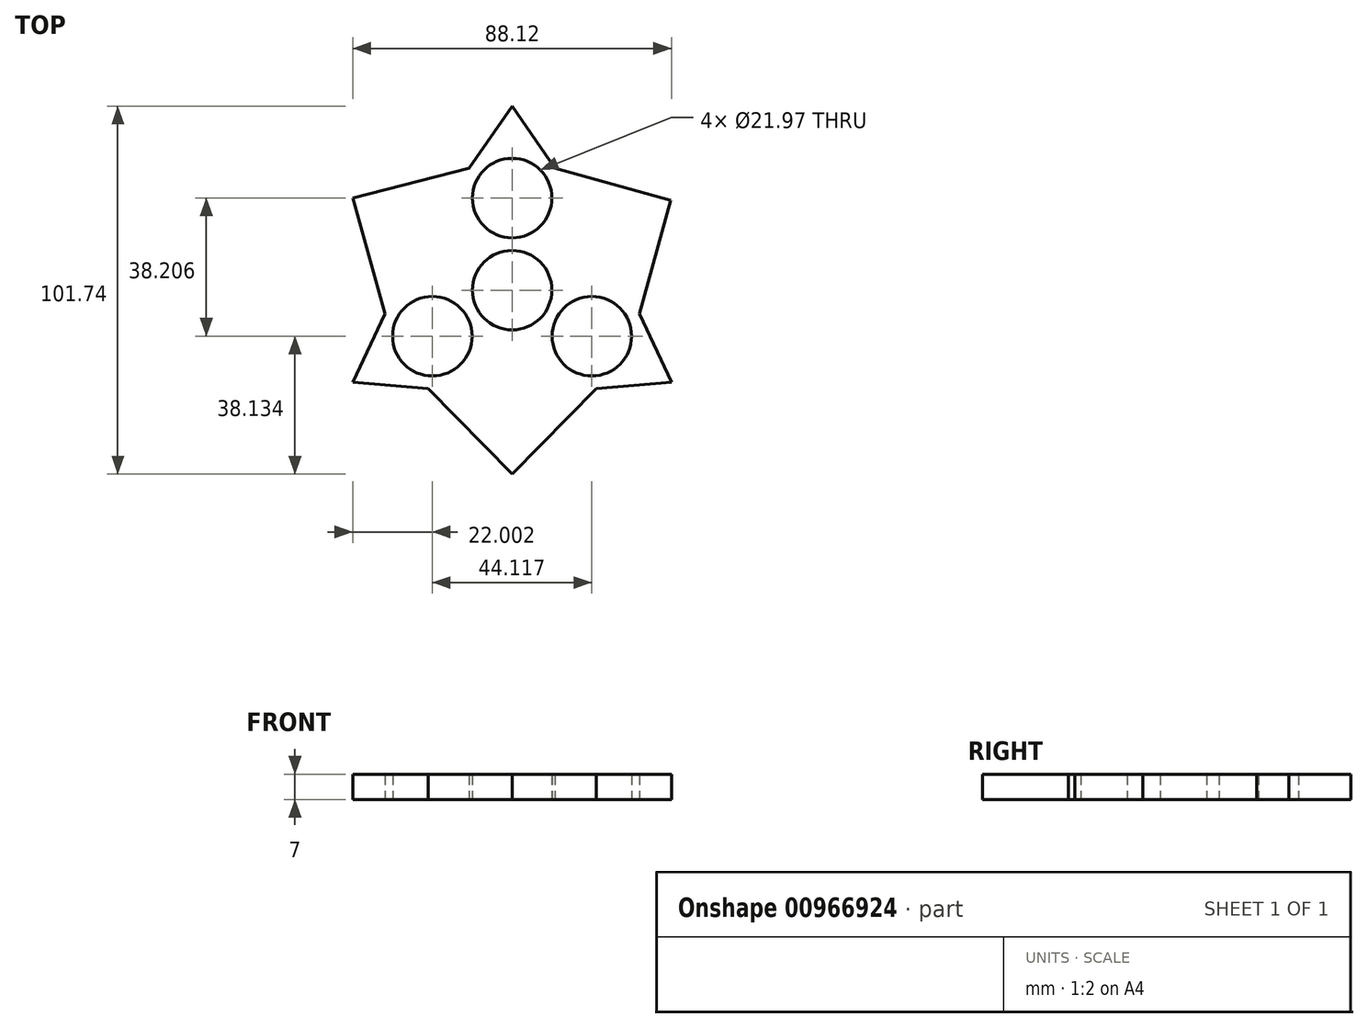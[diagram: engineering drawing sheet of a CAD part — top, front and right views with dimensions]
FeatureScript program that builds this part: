
annotation { "Feature Type Name" : "Feature", "Feature Type Description" : "" }
export const myFeature = defineFeature(function(context is Context, id is Id, definition is map)
    precondition{}
    {
        {
            var Q0;
            Q0=qCreatedBy(makeId("Top.planeOp"),FACE);
            var sketch = newSketch(context, id + "F0", { "sketchPlane" : qUnion([Q0])});
            skCircle(sketch, "E0", {"center": v(0, 0) * mm, "radius": 10.99 * mm});
            skCircle(sketch, "E1", {"center": v(0, 0) * mm, "radius": 25.47 * mm, "construction": true});
            skCircle(sketch, "E2", {"center": v(0, 25.47) * mm, "radius": 10.99 * mm});
            skCircle(sketch, "E3", {"center": v(-22.06, -12.74) * mm, "radius": 10.99 * mm});
            skCircle(sketch, "E4", {"center": v(22.06, -12.74) * mm, "radius": 10.99 * mm});
            skLineSegment(sketch, "E5", {"start": v(-22.06, -12.74) * mm, "end": v(22.06, -12.74) * mm, "construction": true});
            skLineSegment(sketch, "E6", {"start": v(0, 25.47) * mm, "end": v(-22.06, -12.74) * mm, "construction": true});
            skLineSegment(sketch, "E7", {"start": v(22.06, -12.74) * mm, "end": v(0, 25.47) * mm, "construction": true});
            skLineSegment(sketch, "E8.bottom", {"start": v(-57.15, 57.15) * mm, "end": v(57.15, 57.15) * mm, "construction": true});
            skLineSegment(sketch, "E8.top", {"start": v(-57.15, -57.15) * mm, "end": v(57.15, -57.15) * mm, "construction": true});
            skLineSegment(sketch, "E8.left", {"start": v(-57.15, 57.15) * mm, "end": v(-57.15, -57.15) * mm, "construction": true});
            skLineSegment(sketch, "E8.right", {"start": v(57.15, 57.15) * mm, "end": v(57.15, -57.15) * mm, "construction": true});
            skPoint(sketch, "E9", {"position": v(-57.15, 0) * mm});
            skPoint(sketch, "E10", {"position": v(0, 57.15) * mm});
            skSolve(sketch);
        }
        {
            var Q0;
            Q0=qCreatedBy(makeId("Top.planeOp"),FACE);
            var sketch = newSketch(context, id + "F1", { "sketchPlane" : qUnion([Q0])});
            skCircle(sketch, "E11", {"center": v(0, 0) * mm, "radius": 10.99 * mm});
            skCircle(sketch, "E12", {"center": v(-22.06, -12.74) * mm, "radius": 10.99 * mm});
            skCircle(sketch, "E13", {"center": v(0, 25.47) * mm, "radius": 10.99 * mm});
            skCircle(sketch, "E14", {"center": v(22.06, -12.74) * mm, "radius": 10.99 * mm});
            skLineSegment(sketch, "E15.bottom", {"start": v(-57.15, 57.15) * mm, "end": v(57.15, 57.15) * mm, "construction": true});
            skLineSegment(sketch, "E15.top", {"start": v(-57.15, -57.15) * mm, "end": v(57.15, -57.15) * mm, "construction": true});
            skLineSegment(sketch, "E15.left", {"start": v(-57.15, 57.15) * mm, "end": v(-57.15, -57.15) * mm, "construction": true});
            skLineSegment(sketch, "E15.right", {"start": v(57.15, 57.15) * mm, "end": v(57.15, -57.15) * mm, "construction": true});
            skPoint(sketch, "E16", {"position": v(-57.15, 0) * mm});
            skPoint(sketch, "E17", {"position": v(0, 57.15) * mm});
            skCircle(sketch, "E18", {"center": v(0, 25.47) * mm, "radius": 14.49 * mm, "construction": true});
            skCircle(sketch, "E19", {"center": v(22.06, -12.74) * mm, "radius": 14.49 * mm, "construction": true});
            skCircle(sketch, "E20", {"center": v(-22.06, -12.74) * mm, "radius": 14.49 * mm, "construction": true});
            skCircle(sketch, "E21", {"center": v(0, 0) * mm, "radius": 14.49 * mm, "construction": true});
            skLineSegment(sketch, "E22", {"start": v(11.9, 33.73) * mm, "end": v(0, 50.87) * mm});
            skLineSegment(sketch, "E23", {"start": v(0, 50.87) * mm, "end": v(-11.9, 33.73) * mm});
            skLineSegment(sketch, "E24", {"start": v(-11.9, 33.73) * mm, "end": v(-44.06, 25.44) * mm});
            skLineSegment(sketch, "E25", {"start": v(35.16, -6.56) * mm, "end": v(43.86, 24.9) * mm});
            skLineSegment(sketch, "E26", {"start": v(43.86, 24.9) * mm, "end": v(11.9, 33.73) * mm});
            skCircle(sketch, "E27", {"center": v(0, 0) * mm, "radius": 50.87 * mm, "construction": true});
            skLineSegment(sketch, "E28", {"start": v(0, 25.47) * mm, "end": v(0, 50.87) * mm, "construction": true});
            skLineSegment(sketch, "E29", {"start": v(0, -50.87) * mm, "end": v(23.26, -27.17) * mm});
            skLineSegment(sketch, "E30", {"start": v(-44.06, 25.44) * mm, "end": v(-35.16, -6.56) * mm});
            skLineSegment(sketch, "E31", {"start": v(-35.16, -6.56) * mm, "end": v(-44.06, -25.44) * mm});
            skLineSegment(sketch, "E32", {"start": v(-44.06, -25.44) * mm, "end": v(-23.26, -27.17) * mm});
            skLineSegment(sketch, "E33", {"start": v(-23.26, -27.17) * mm, "end": v(0, -50.87) * mm});
            skLineSegment(sketch, "E34", {"start": v(0, 0) * mm, "end": v(22.06, -12.74) * mm, "construction": true});
            skLineSegment(sketch, "E35", {"start": v(23.26, -27.17) * mm, "end": v(44.06, -25.44) * mm});
            skLineSegment(sketch, "E36", {"start": v(44.06, -25.44) * mm, "end": v(35.16, -6.56) * mm});
            skLineSegment(sketch, "E37", {"start": v(-44.06, -25.44) * mm, "end": v(-22.06, -12.74) * mm, "construction": true});
            skLineSegment(sketch, "E38", {"start": v(0, 0) * mm, "end": v(-22.06, -12.74) * mm, "construction": true});
            skLineSegment(sketch, "E39", {"start": v(22.06, -12.74) * mm, "end": v(44.06, -25.44) * mm, "construction": true});
            skSolve(sketch);
        }
        {
            var Q0;
            Q0 = qSketchRegion(id + "F1", true);
            extrude(context, id + "F2", {"entities" : qUnion([Q0]), "depth" : 7 * mm, "offsetDistance" : 25.4 * mm});
        }
    });
